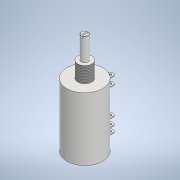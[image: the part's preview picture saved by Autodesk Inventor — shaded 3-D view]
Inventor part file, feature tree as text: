
AUTODESK INVENTOR PART (.ipt)
format: ipt  version: 2022.3 (Build 263350000, 350)  size: 257,024 bytes
history: native  units: mm
features: extrude x11, sketch x7, fillet x2, thread x1
ambient origin geometry x8: Origin, YZ Plane, XZ Plane, XY Plane, X Axis, Y Axis, Z Axis, Center Point
bodies: Solid1 (feature_tree)
feature tree (21):
  sketch  "Sketch1"  dims[d0=20.5mm d1=5.0mm]
  extrude  "Extrusion1"  Depth=5.0mm
  extrude  "Extrusion2"  Depth=36.0mm TaperAngle=0.0deg
  extrude  "Extrusion3"  Depth=4.0mm TaperAngle=0.0deg
  thread  "Thread1"  [1 undecoded]
  extrude  "Extrusion4"  Depth=9.0mm TaperAngle=0.0deg
  fillet  "Fillet1"  Radius=1.0mm
  extrude  "Extrusion5"  Depth=4.0mm TaperAngle=0.0deg
  extrude  "Extrusion6"  Depth=33.5mm TaperAngle=0.0deg
  sketch  "Sketch5"  dims[d14=4.0mm d15=1.2mm d16=0.0mm]
  extrude  "Extrusion7"  Depth=5.0mm
  extrude  "Extrusion8"  Depth=0.5mm
  sketch  "Sketch6"  dims[d17=0.2mm d18=33.5mm d19=0.0mm]
  extrude  "Extrusion9"  Depth=5.0mm
  extrude  "Extrusion10"  Depth=8.0mm
  extrude  "Extrusion11"  Depth=5.0mm
  fillet  "Fillet2"  Radius=0.5mm
  sketch  "Sketch2"  dims[d2=2.0mm d3=36.0mm d4=0.0mm]
  sketch  "Sketch3"  dims[d5=8.0mm d6=9.0mm d7=0.0mm d8=4.0mm]
  sketch  "Sketch4"  dims[d9=13.0mm d10=0.0mm d11=9.0mm d12=0.0mm d13=1.0mm]
  sketch  "Sketch7"  dims[d20=2.5mm d21=0.0mm d22=5.0mm d23=0.5mm d24=5.0mm d25=8.0mm d26=5.0mm d27=0.5mm d28=5.0mm d29=5.0mm d30=5.0mm d31=0.5mm d32=5.0mm d33=8.0mm d34=5.0mm d35=5.0mm d36=5.0mm d37=0.5mm d38=5.0mm d39=0.5mm d40=5.0mm d41=0.0mm d42=5.0mm d43=0.0mm d44=1.5mm d45=180.0deg d46=3.0mm d47=1.0mm d48=1.5mm d49=1.5mm d50=10.0mm d51=0.0mm d52=10.0mm d53=0.0mm d54=10.0mm d55=0.75mm d56=0.0mm d57=0.75mm]
note: 1 required parameter value undecoded (feature->parameter linkage not recoverable at this tier; creation-order binding heuristic only, values carry confidence <= 0.55)
